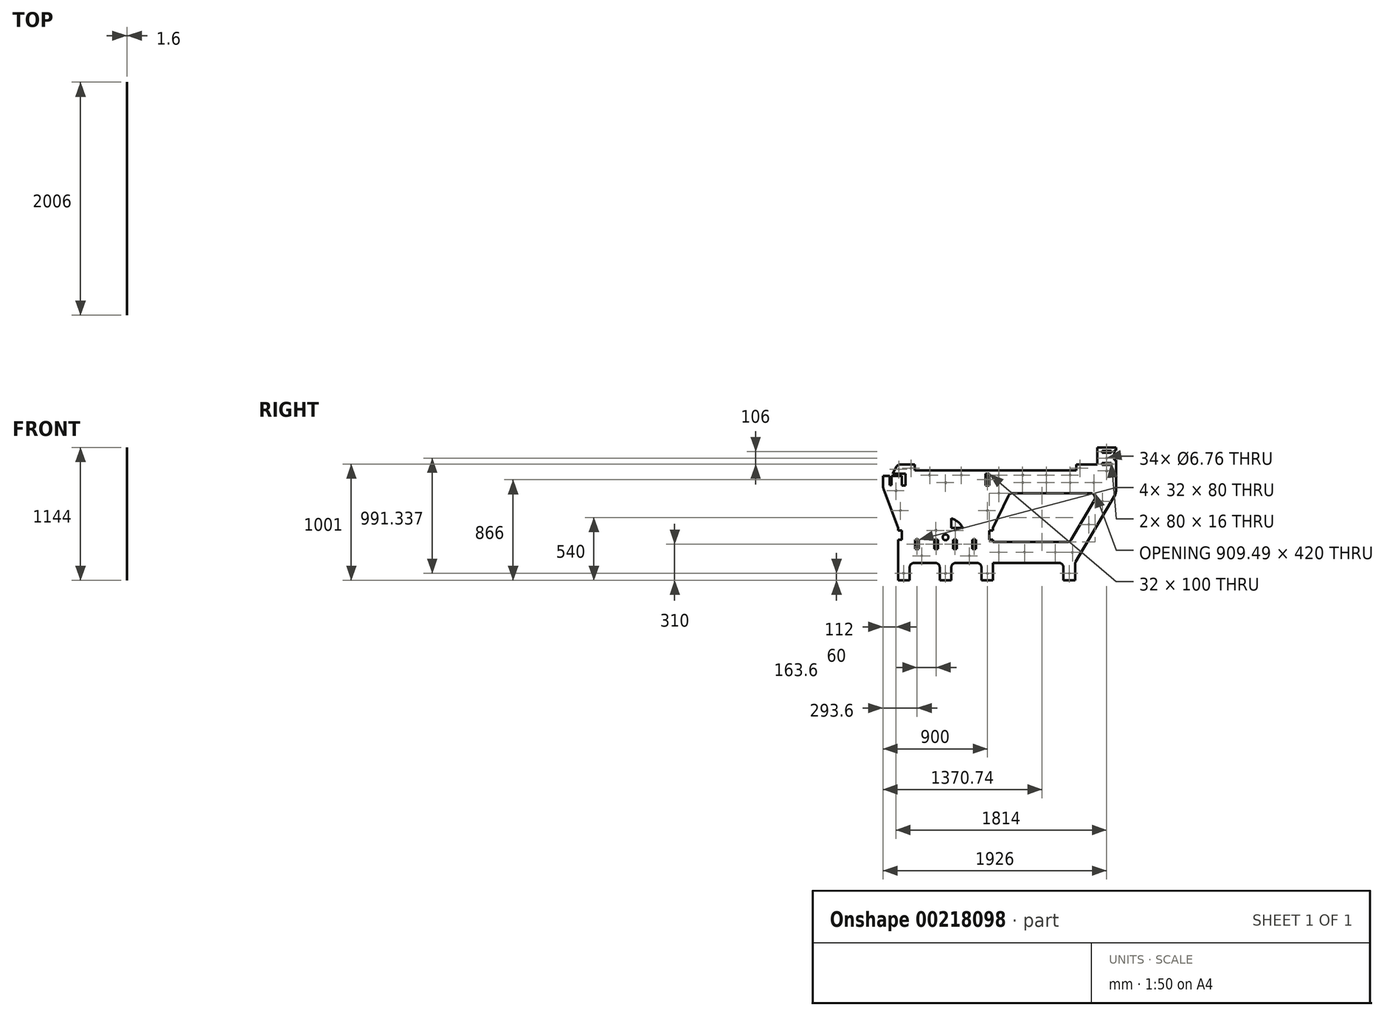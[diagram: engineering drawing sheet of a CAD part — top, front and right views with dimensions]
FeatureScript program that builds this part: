
annotation { "Feature Type Name" : "Feature", "Feature Type Description" : "" }
export const myFeature = defineFeature(function(context is Context, id is Id, definition is map)
    precondition{}
    {
        {
            assignVariable(context, id + "F0", {"name" : "grueso", "anyValue" : 1.6});
        }
        {
            var Q0;
            Q0=qCreatedBy(makeId("Right.planeOp"),FACE);
            var sketch = newSketch(context, id + "F1", { "sketchPlane" : qUnion([Q0])});
            skLineSegment(sketch, "E0.bottom", {"start": v(0, 0) * mm, "end": v(818, 0) * mm});
            skLineSegment(sketch, "E0.top", {"start": v(0, 900) * mm, "end": v(818, 900) * mm});
            skLineSegment(sketch, "E0.left", {"start": v(0, 0) * mm, "end": v(0, 900) * mm});
            skLineSegment(sketch, "E0.right", {"start": v(818, 0) * mm, "end": v(818, 900) * mm});
            skPoint(sketch, "E0.middle", {"position": v(409, 450) * mm});
            skLineSegment(sketch, "E1", {"start": v(100, 0) * mm, "end": v(100, 110) * mm});
            skLineSegment(sketch, "E2", {"start": v(140, 750) * mm, "end": v(678, 750) * mm});
            skLineSegment(sketch, "E3", {"start": v(718, 710) * mm, "end": v(718, 490) * mm});
            skPoint(sketch, "E4.visualSharp", {"position": v(100, 750) * mm});
            skArc(sketch, "E4.filletArc", {"start": v(140, 750) * mm, "mid": v(111.72, 738.28) * mm, "end": v(100, 710) * mm});
            skPoint(sketch, "E5.visualSharp", {"position": v(718, 750) * mm});
            skArc(sketch, "E5.filletArc", {"start": v(718, 710) * mm, "mid": v(706.28, 738.28) * mm, "end": v(678, 750) * mm});
            skLineSegment(sketch, "E6", {"start": v(678, 450) * mm, "end": v(619.82, 450) * mm});
            skLineSegment(sketch, "E7", {"start": v(678, 150) * mm, "end": v(626.89, 150) * mm});
            skLineSegment(sketch, "E8", {"start": v(32, 900) * mm, "end": v(32, 816) * mm});
            skLineSegment(sketch, "E9", {"start": v(32, 816) * mm, "end": v(64, 816) * mm});
            skLineSegment(sketch, "E10", {"start": v(64, 816) * mm, "end": v(64, 900) * mm});
            skLineSegment(sketch, "E11", {"start": v(409, -66.66) * mm, "end": v(409, 936.4) * mm, "construction": true});
            skPoint(sketch, "E11.endSnap0", {"position": v(409, 0) * mm});
            skLineSegment(sketch, "E12.trimOffspring", {"start": v(100, 490) * mm, "end": v(100, 710) * mm});
            skLineSegment(sketch, "E13.trimOffspring", {"start": v(718, 110) * mm, "end": v(718, 0) * mm});
            skPoint(sketch, "E14.visualSharp", {"position": v(718, 450) * mm});
            skArc(sketch, "E14.filletArc", {"start": v(678, 450) * mm, "mid": v(706.28, 461.72) * mm, "end": v(718, 490) * mm});
            skPoint(sketch, "E15.visualSharp", {"position": v(100, 450) * mm});
            skArc(sketch, "E15.filletArc", {"start": v(100, 490) * mm, "mid": v(111.72, 461.72) * mm, "end": v(140, 450) * mm});
            skPoint(sketch, "E16.visualSharp", {"position": v(100, 150) * mm});
            skArc(sketch, "E16.filletArc", {"start": v(140, 150) * mm, "mid": v(111.72, 138.28) * mm, "end": v(100, 110) * mm});
            skPoint(sketch, "E17.visualSharp", {"position": v(718, 150) * mm});
            skArc(sketch, "E17.filletArc", {"start": v(718, 110) * mm, "mid": v(706.28, 138.28) * mm, "end": v(678, 150) * mm});
            skLineSegment(sketch, "E18.MirrorCS", {"start": v(754, 816) * mm, "end": v(754, 900) * mm});
            skLineSegment(sketch, "E19.MirrorCS", {"start": v(786, 900) * mm, "end": v(786, 816) * mm});
            skLineSegment(sketch, "E20.MirrorCS", {"start": v(786, 816) * mm, "end": v(754, 816) * mm});
            skLineSegment(sketch, "E21.trimOffspring", {"start": v(603.68, 450) * mm, "end": v(140, 450) * mm});
            skLineSegment(sketch, "E22.trimOffspring", {"start": v(562.94, 150) * mm, "end": v(140, 150) * mm});
            skLineSegment(sketch, "E23", {"start": v(359, 61.01) * mm, "end": v(359, 0) * mm});
            skLineSegment(sketch, "E24", {"start": v(459, 110) * mm, "end": v(459, 0) * mm});
            skPoint(sketch, "E25.endSnap0", {"position": v(409, 900) * mm});
            skLineSegment(sketch, "E26", {"start": v(603.68, 450) * mm, "end": v(619.82, 450) * mm});
            skLineSegment(sketch, "E27", {"start": v(319, 150) * mm, "end": v(562.94, 150) * mm});
            skLineSegment(sketch, "E28", {"start": v(359, 110) * mm, "end": v(359, 61.01) * mm});
            skLineSegment(sketch, "E29", {"start": v(459, 110) * mm, "end": v(459, 110) * mm});
            skLineSegment(sketch, "E30", {"start": v(499, 150) * mm, "end": v(626.89, 150) * mm});
            skCircle(sketch, "E31", {"center": v(409, 370) * mm, "radius": 25 * mm});
            skPoint(sketch, "E32.visualSharp", {"position": v(459, 150) * mm});
            skArc(sketch, "E32.filletArc", {"start": v(499, 150) * mm, "mid": v(470.72, 138.28) * mm, "end": v(459, 110) * mm});
            skPoint(sketch, "E33.visualSharp", {"position": v(359, 150) * mm});
            skArc(sketch, "E33.filletArc", {"start": v(359, 110) * mm, "mid": v(347.28, 138.28) * mm, "end": v(319, 150) * mm});
            skLineSegment(sketch, "E34.bottom", {"start": v(32, 350) * mm, "end": v(0, 350) * mm});
            skLineSegment(sketch, "E34.top", {"start": v(32, 430) * mm, "end": v(0, 430) * mm});
            skLineSegment(sketch, "E34.left", {"start": v(32, 350) * mm, "end": v(32, 430) * mm});
            skLineSegment(sketch, "E34.right", {"start": v(0, 350) * mm, "end": v(0, 430) * mm});
            skLineSegment(sketch, "E35.MirrorCS", {"start": v(786, 350) * mm, "end": v(786, 430) * mm});
            skLineSegment(sketch, "E36.MirrorCS", {"start": v(786, 430) * mm, "end": v(818, 430) * mm});
            skLineSegment(sketch, "E37.MirrorCS", {"start": v(818, 350) * mm, "end": v(818, 430) * mm});
            skLineSegment(sketch, "E38.MirrorCS", {"start": v(786, 350) * mm, "end": v(818, 350) * mm});
            skLineSegment(sketch, "E39.bottom", {"start": v(179.6, 270) * mm, "end": v(147.6, 270) * mm});
            skLineSegment(sketch, "E39.top", {"start": v(179.6, 350) * mm, "end": v(147.6, 350) * mm});
            skLineSegment(sketch, "E39.left", {"start": v(179.6, 270) * mm, "end": v(179.6, 350) * mm});
            skLineSegment(sketch, "E39.right", {"start": v(147.6, 270) * mm, "end": v(147.6, 350) * mm});
            skPoint(sketch, "E39.middle", {"position": v(163.6, 310) * mm});
            skLineSegment(sketch, "E40", {"start": v(359, 750) * mm, "end": v(359, 450) * mm});
            skLineSegment(sketch, "E41", {"start": v(459, 750) * mm, "end": v(459, 450) * mm});
            skArc(sketch, "E42", {"start": v(359, 532.48) * mm, "mid": v(300.83, 501.15) * mm, "end": v(259, 450) * mm});
            skArc(sketch, "E43", {"start": v(459, 532.48) * mm, "mid": v(517.17, 501.15) * mm, "end": v(559, 450) * mm});
            skLineSegment(sketch, "E44.bottom", {"start": v(311.2, 270) * mm, "end": v(343.2, 270) * mm});
            skLineSegment(sketch, "E44.top", {"start": v(311.2, 350) * mm, "end": v(343.2, 350) * mm});
            skLineSegment(sketch, "E44.left", {"start": v(311.2, 270) * mm, "end": v(311.2, 350) * mm});
            skLineSegment(sketch, "E44.right", {"start": v(343.2, 270) * mm, "end": v(343.2, 350) * mm});
            skPoint(sketch, "E44.middle", {"position": v(327.2, 310) * mm});
            skPoint(sketch, "E45.cornerSnap0", {"position": v(327.2, 270) * mm});
            skLineSegment(sketch, "E46.bottom", {"start": v(474.8, 270) * mm, "end": v(506.8, 270) * mm});
            skLineSegment(sketch, "E46.top", {"start": v(474.8, 350) * mm, "end": v(506.8, 350) * mm});
            skLineSegment(sketch, "E46.left", {"start": v(474.8, 270) * mm, "end": v(474.8, 350) * mm});
            skLineSegment(sketch, "E46.right", {"start": v(506.8, 270) * mm, "end": v(506.8, 350) * mm});
            skPoint(sketch, "E46.middle", {"position": v(490.8, 310) * mm});
            skLineSegment(sketch, "E47.bottom", {"start": v(638.4, 270) * mm, "end": v(670.4, 270) * mm});
            skLineSegment(sketch, "E47.top", {"start": v(638.4, 350) * mm, "end": v(670.4, 350) * mm});
            skLineSegment(sketch, "E47.left", {"start": v(638.4, 270) * mm, "end": v(638.4, 350) * mm});
            skLineSegment(sketch, "E47.right", {"start": v(670.4, 270) * mm, "end": v(670.4, 350) * mm});
            skPoint(sketch, "E47.middle", {"position": v(654.4, 310) * mm});
            skLineSegment(sketch, "E48", {"start": v(818, 900) * mm, "end": v(1876, 900) * mm});
            skLineSegment(sketch, "E49", {"start": v(1876, 900) * mm, "end": v(1876, 760.86) * mm});
            skLineSegment(sketch, "E50", {"start": v(1870.5, 740.63) * mm, "end": v(1529.72, 159.37) * mm});
            skLineSegment(sketch, "E51", {"start": v(1524.23, 139.14) * mm, "end": v(1524.23, 0) * mm});
            skLineSegment(sketch, "E52", {"start": v(1524.23, 0) * mm, "end": v(1424.23, 0) * mm});
            skLineSegment(sketch, "E53", {"start": v(1424.23, 0) * mm, "end": v(1424.23, 110) * mm});
            skLineSegment(sketch, "E54", {"start": v(1690, 689.77) * mm, "end": v(1490.66, 349.77) * mm});
            skLineSegment(sketch, "E55", {"start": v(1456.15, 330) * mm, "end": v(818, 330) * mm});
            skLineSegment(sketch, "E56", {"start": v(949.82, 727.18) * mm, "end": v(818, 450) * mm});
            skPoint(sketch, "E57.visualSharp", {"position": v(1716.3, 734.63) * mm});
            skArc(sketch, "E57.filletArc", {"start": v(1690, 689.77) * mm, "mid": v(1690.2, 729.88) * mm, "end": v(1655.49, 750) * mm});
            skPoint(sketch, "E58.visualSharp", {"position": v(1424.23, 150) * mm});
            skArc(sketch, "E58.filletArc", {"start": v(1424.23, 110) * mm, "mid": v(1412.51, 138.28) * mm, "end": v(1384.23, 150) * mm});
            skPoint(sketch, "E59.visualSharp", {"position": v(1524.23, 150) * mm});
            skArc(sketch, "E59.filletArc", {"start": v(1529.72, 159.37) * mm, "mid": v(1525.63, 149.62) * mm, "end": v(1524.23, 139.14) * mm});
            skPoint(sketch, "E60.visualSharp", {"position": v(1876, 750) * mm});
            skArc(sketch, "E60.filletArc", {"start": v(1870.5, 740.63) * mm, "mid": v(1874.6, 750.38) * mm, "end": v(1876, 760.86) * mm});
            skArc(sketch, "E61.filletArc", {"start": v(1456.15, 330) * mm, "mid": v(1476.03, 335.3) * mm, "end": v(1490.66, 349.77) * mm});
            skLineSegment(sketch, "E62", {"start": v(1384.23, 150) * mm, "end": v(818, 150) * mm});
            skLineSegment(sketch, "E63", {"start": v(818, 450) * mm, "end": v(818, 330) * mm});
            skLineSegment(sketch, "E64", {"start": v(985.94, 750) * mm, "end": v(1655.49, 750) * mm});
            skPoint(sketch, "E65.visualSharp", {"position": v(960.67, 750) * mm});
            skArc(sketch, "E65.filletArc", {"start": v(985.94, 750) * mm, "mid": v(964.58, 743.82) * mm, "end": v(949.82, 727.18) * mm});
            skLineSegment(sketch, "E66", {"start": v(0, 900) * mm, "end": v(-130, 900) * mm});
            skLineSegment(sketch, "E67", {"start": v(-130, 900) * mm, "end": v(-130, 821.57) * mm});
            skPoint(sketch, "E68", {"position": v(0, 450) * mm});
            skLineSegment(sketch, "E69", {"start": v(-122.5, 779.78) * mm, "end": v(0, 450) * mm});
            skPoint(sketch, "E70.visualSharp", {"position": v(-130, 800) * mm});
            skArc(sketch, "E70.filletArc", {"start": v(-130, 821.57) * mm, "mid": v(-128.1, 800.34) * mm, "end": v(-122.5, 779.78) * mm});
            skLineSegment(sketch, "E71.bottom", {"start": v(-57, 820) * mm, "end": v(-73, 820) * mm});
            skLineSegment(sketch, "E71.top", {"start": v(-57, 900) * mm, "end": v(-73, 900) * mm});
            skLineSegment(sketch, "E71.left", {"start": v(-57, 820) * mm, "end": v(-57, 900) * mm});
            skLineSegment(sketch, "E71.right", {"start": v(-73, 820) * mm, "end": v(-73, 900) * mm});
            skPoint(sketch, "E71.middle", {"position": v(-65, 860) * mm});
            skLineSegment(sketch, "E72", {"start": v(15.91, 996) * mm, "end": v(143, 996) * mm});
            skLineSegment(sketch, "E73", {"start": v(786, 946) * mm, "end": v(1876, 946) * mm});
            skLineSegment(sketch, "E74", {"start": v(1876, 946) * mm, "end": v(1876, 900) * mm});
            skLineSegment(sketch, "E75", {"start": v(-48, 916) * mm, "end": v(-10, 981.12) * mm});
            skPoint(sketch, "E76.visualSharp", {"position": v(-1.32, 996) * mm});
            skArc(sketch, "E76.filletArc", {"start": v(15.91, 996) * mm, "mid": v(0.97, 992.02) * mm, "end": v(-10, 981.12) * mm});
            skLineSegment(sketch, "E77", {"start": v(143, 996) * mm, "end": v(143, 900) * mm});
            skLineSegment(sketch, "E78", {"start": v(143, 946) * mm, "end": v(754, 946) * mm});
            skLineSegment(sketch, "E79", {"start": v(754, 946) * mm, "end": v(786, 946) * mm});
            skLineSegment(sketch, "E80", {"start": v(786, 916) * mm, "end": v(786, 900) * mm});
            skLineSegment(sketch, "E81", {"start": v(754, 916) * mm, "end": v(754, 900) * mm});
            skLineSegment(sketch, "E82", {"start": v(754, 916) * mm, "end": v(786, 916) * mm});
            skLineSegment(sketch, "E83", {"start": v(1876, 946) * mm, "end": v(1876, 1160) * mm});
            skLineSegment(sketch, "E84", {"start": v(1876, 1160) * mm, "end": v(1716, 1160) * mm});
            skLineSegment(sketch, "E85", {"start": v(1716, 1160) * mm, "end": v(1716, 946) * mm});
            skLineSegment(sketch, "E86", {"start": v(-48, 916) * mm, "end": v(64, 916) * mm});
            skLineSegment(sketch, "E87", {"start": v(64, 916) * mm, "end": v(64, 900) * mm});
            skLineSegment(sketch, "E88", {"start": v(1716, 996) * mm, "end": v(1536, 996) * mm});
            skLineSegment(sketch, "E89", {"start": v(1536, 996) * mm, "end": v(1536, 946) * mm});
            skLineSegment(sketch, "E90", {"start": v(1756, 993) * mm, "end": v(1836, 993) * mm});
            skLineSegment(sketch, "E91", {"start": v(1836, 993) * mm, "end": v(1836, 1009) * mm});
            skLineSegment(sketch, "E92", {"start": v(1836, 1009) * mm, "end": v(1756, 1009) * mm});
            skLineSegment(sketch, "E93", {"start": v(1756, 1009) * mm, "end": v(1756, 993) * mm});
            skLineSegment(sketch, "E94", {"start": v(1756, 1099) * mm, "end": v(1836, 1099) * mm});
            skLineSegment(sketch, "E95", {"start": v(1836, 1099) * mm, "end": v(1836, 1115) * mm});
            skLineSegment(sketch, "E96", {"start": v(1836, 1115) * mm, "end": v(1756, 1115) * mm});
            skLineSegment(sketch, "E97", {"start": v(1756, 1115) * mm, "end": v(1756, 1099) * mm});
            skLineSegment(sketch, "E98", {"start": v(1716, 1144) * mm, "end": v(1876, 1144) * mm});
            skLineSegment(sketch, "E99", {"start": v(1876, 1116.5) * mm, "end": v(1860, 1116.5) * mm});
            skLineSegment(sketch, "E100", {"start": v(1860, 1116.5) * mm, "end": v(1860, 1036.5) * mm});
            skLineSegment(sketch, "E101", {"start": v(1860, 1036.5) * mm, "end": v(1876, 1036.5) * mm});
            skSolve(sketch);
        }
        {
            var Q0;
            {var subQ5=sQuery(id+"F1.wireOp",EDGE,"E48");Q0=makeQuery(id+"F1.imprint","IMPRINT",FACE,{"disambiguationData":[TD([[makeQuery(id+"F1.imprint","IMPRINT",EDGE,{"derivedFrom":subQ5}),-1.0]])]});}
            var Q1;
            {var subQ1=sQuery(id+"F1.wireOp",EDGE,"E23");Q1=makeQuery(id+"F1.imprint","IMPRINT",FACE,{"disambiguationData":[TD([[makeQuery(id+"F1.imprint","IMPRINT",EDGE,{"derivedFrom":subQ1}),1.0]])]});}
            var Q2;
            {var subQ34=sQuery(id+"F1.wireOp",EDGE,"E1");Q2=makeQuery(id+"F1.imprint","IMPRINT",FACE,{"disambiguationData":[TD([[makeQuery(id+"F1.imprint","IMPRINT",EDGE,{"derivedFrom":subQ34}),1.0]])]});}
            var Q3;
            {var subQ3=sQuery(id+"F1.wireOp",EDGE,"E42");Q3=makeQuery(id+"F1.imprint","IMPRINT",FACE,{"disambiguationData":[TD([[makeQuery(id+"F1.imprint","IMPRINT",EDGE,{"derivedFrom":subQ3}),1.0]])]});}
            var Q4;
            {var subQ3=sQuery(id+"F1.wireOp",EDGE,"E43");Q4=makeQuery(id+"F1.imprint","IMPRINT",FACE,{"disambiguationData":[TD([[makeQuery(id+"F1.imprint","IMPRINT",EDGE,{"derivedFrom":subQ3}),-1.0]])]});}
            var Q5;
            {var subQ0=sQuery(id+"F1.wireOp",EDGE,"E40");var subQ4=sQuery(id+"F1.wireOp",EDGE,"E2");var subQ5=makeQuery(id+"F1.imprint","INTERSECT",VERTEX,{"derivedFrom":[subQ4,subQ0]});Q5=makeQuery(id+"F1.imprint","IMPRINT",FACE,{"disambiguationData":[TD([[makeQuery(id+"F1.imprint","IMPRINT",EDGE,{"disambiguationData":[TD([[subQ5,-1.0]])],"derivedFrom":subQ4}),-1.0]])]});}
            var Q6;
            {var subQ1=sQuery(id+"F1.wireOp",EDGE,"E66");Q6=makeQuery(id+"F1.imprint","IMPRINT",FACE,{"disambiguationData":[TD([[makeQuery(id+"F1.imprint","IMPRINT",EDGE,{"derivedFrom":subQ1}),1.0]])]});}
            var Q7;
            {var subQ0=sQuery(id+"F1.wireOp",EDGE,"8OQY55YS-XfRK-lt9R-q8WZ-AcM36SrQRaeO");Q7=makeQuery(id+"F1.imprint","IMPRINT",FACE,{"disambiguationData":[TD([[makeQuery(id+"F1.imprint","IMPRINT",EDGE,{"derivedFrom":subQ0}),-1.0]])]});}
            var Q8;
            {var subQ1=sQuery(id+"F1.wireOp",EDGE,"E48");Q8=makeQuery(id+"F1.imprint","IMPRINT",FACE,{"disambiguationData":[TD([[makeQuery(id+"F1.imprint","IMPRINT",EDGE,{"derivedFrom":subQ1}),1.0]])]});}
            var Q9;
            {var subQ4=sQuery(id+"F1.wireOp",EDGE,"E78");Q9=makeQuery(id+"F1.imprint","IMPRINT",FACE,{"disambiguationData":[TD([[makeQuery(id+"F1.imprint","IMPRINT",EDGE,{"derivedFrom":subQ4}),-1.0]])]});}
            var Q10;
            {var subQ0=sQuery(id+"F1.wireOp",EDGE,"E72");Q10=makeQuery(id+"F1.imprint","IMPRINT",FACE,{"disambiguationData":[TD([[makeQuery(id+"F1.imprint","IMPRINT",EDGE,{"derivedFrom":subQ0}),-1.0]])]});}
            var Q11;
            {var subQ4=sQuery(id+"F1.wireOp",EDGE,"E88");Q11=makeQuery(id+"F1.imprint","IMPRINT",FACE,{"disambiguationData":[TD([[makeQuery(id+"F1.imprint","IMPRINT",EDGE,{"derivedFrom":subQ4}),1.0]])]});}
            var Q12;
            {var subQ0=sQuery(id+"F1.wireOp",EDGE,"E4.filletArc");Q12=makeQuery(id+"F1.imprint","IMPRINT",FACE,{"disambiguationData":[TD([[makeQuery(id+"F1.imprint","IMPRINT",EDGE,{"derivedFrom":subQ0}),1.0]])]});}
            var Q13;
            Q13=makeQuery(id+"F1.imprint","IMPRINT",FACE,{"disambiguationData":[TD([[makeQuery(id+"F1.imprint","IMPRINT",EDGE,{"derivedFrom":sQuery(id+"F1.wireOp",EDGE,"E3")}),-1.0]])]});
            var Q14;
            Q14=makeQuery(id+"F1.imprint","IMPRINT",FACE,{"disambiguationData":[TD([[makeQuery(id+"F1.imprint","IMPRINT",EDGE,{"derivedFrom":sQuery(id+"F1.wireOp",EDGE,"E90")}),-1.0]])]});
            extrude(context, id + "F2", {"entities" : qUnion([Q0, Q1, Q2, Q3, Q4, Q5, Q6, Q7, Q8, Q9, Q10, Q11, Q12, Q13, Q14]), "depth" : (getVariable(context, 'grueso')) * mm});
        }
        {
            var Q0;
            Q0=makeQuery(id+"F2.opExtrude","CAP_FACE",FACE,{"disambiguationData":[OSD([sQuery(id+"F1.wireOp",EDGE,"E0.bottom"),sQuery(id+"F1.wireOp",EDGE,"E0.top"),sQuery(id+"F1.wireOp",EDGE,"E0.left"),sQuery(id+"F1.wireOp",EDGE,"E0.right"),sQuery(id+"F1.wireOp",EDGE,"E1"),sQuery(id+"F1.wireOp",EDGE,"E2"),sQuery(id+"F1.wireOp",EDGE,"E3"),sQuery(id+"F1.wireOp",EDGE,"E4.filletArc"),sQuery(id+"F1.wireOp",EDGE,"E5.filletArc"),sQuery(id+"F1.wireOp",EDGE,"E6"),sQuery(id+"F1.wireOp",EDGE,"E7"),sQuery(id+"F1.wireOp",EDGE,"E8"),sQuery(id+"F1.wireOp",EDGE,"E9"),sQuery(id+"F1.wireOp",EDGE,"E10"),sQuery(id+"F1.wireOp",EDGE,"E12.trimOffspring"),sQuery(id+"F1.wireOp",EDGE,"E13.trimOffspring"),sQuery(id+"F1.wireOp",EDGE,"E14.filletArc"),sQuery(id+"F1.wireOp",EDGE,"E15.filletArc"),sQuery(id+"F1.wireOp",EDGE,"E16.filletArc"),sQuery(id+"F1.wireOp",EDGE,"E17.filletArc"),sQuery(id+"F1.wireOp",EDGE,"E18.MirrorCS"),sQuery(id+"F1.wireOp",EDGE,"E19.MirrorCS"),sQuery(id+"F1.wireOp",EDGE,"E20.MirrorCS"),sQuery(id+"F1.wireOp",EDGE,"E21.trimOffspring"),sQuery(id+"F1.wireOp",EDGE,"E22.trimOffspring"),sQuery(id+"F1.wireOp",EDGE,"E23"),sQuery(id+"F1.wireOp",EDGE,"E24"),sQuery(id+"F1.wireOp",EDGE,"E26"),sQuery(id+"F1.wireOp",EDGE,"E28"),sQuery(id+"F1.wireOp",EDGE,"E30"),sQuery(id+"F1.wireOp",EDGE,"E31"),sQuery(id+"F1.wireOp",EDGE,"E32.filletArc"),sQuery(id+"F1.wireOp",EDGE,"E33.filletArc"),sQuery(id+"F1.wireOp",EDGE,"E34.bottom"),sQuery(id+"F1.wireOp",EDGE,"E34.top"),sQuery(id+"F1.wireOp",EDGE,"E34.left"),sQuery(id+"F1.wireOp",EDGE,"E35.MirrorCS"),sQuery(id+"F1.wireOp",EDGE,"E36.MirrorCS"),sQuery(id+"F1.wireOp",EDGE,"E38.MirrorCS"),sQuery(id+"F1.wireOp",EDGE,"E39.bottom"),sQuery(id+"F1.wireOp",EDGE,"E39.top"),sQuery(id+"F1.wireOp",EDGE,"E39.left"),sQuery(id+"F1.wireOp",EDGE,"E39.right"),sQuery(id+"F1.wireOp",EDGE,"E40"),sQuery(id+"F1.wireOp",EDGE,"E41"),sQuery(id+"F1.wireOp",EDGE,"E42"),sQuery(id+"F1.wireOp",EDGE,"E43"),sQuery(id+"F1.wireOp",EDGE,"E44.bottom"),sQuery(id+"F1.wireOp",EDGE,"E44.top"),sQuery(id+"F1.wireOp",EDGE,"E44.left"),sQuery(id+"F1.wireOp",EDGE,"E44.right"),sQuery(id+"F1.wireOp",EDGE,"E46.bottom"),sQuery(id+"F1.wireOp",EDGE,"E46.top"),sQuery(id+"F1.wireOp",EDGE,"E46.left"),sQuery(id+"F1.wireOp",EDGE,"E46.right"),sQuery(id+"F1.wireOp",EDGE,"E47.bottom"),sQuery(id+"F1.wireOp",EDGE,"E47.top"),sQuery(id+"F1.wireOp",EDGE,"E47.left"),sQuery(id+"F1.wireOp",EDGE,"E47.right"),sQuery(id+"F1.wireOp",EDGE,"E49"),sQuery(id+"F1.wireOp",EDGE,"E50"),sQuery(id+"F1.wireOp",EDGE,"E51"),sQuery(id+"F1.wireOp",EDGE,"E52"),sQuery(id+"F1.wireOp",EDGE,"E53"),sQuery(id+"F1.wireOp",EDGE,"E54"),sQuery(id+"F1.wireOp",EDGE,"E55"),sQuery(id+"F1.wireOp",EDGE,"E56"),sQuery(id+"F1.wireOp",EDGE,"E57.filletArc"),sQuery(id+"F1.wireOp",EDGE,"E58.filletArc"),sQuery(id+"F1.wireOp",EDGE,"E59.filletArc"),sQuery(id+"F1.wireOp",EDGE,"E60.filletArc"),sQuery(id+"F1.wireOp",EDGE,"E61.filletArc"),sQuery(id+"F1.wireOp",EDGE,"E62"),sQuery(id+"F1.wireOp",EDGE,"E63"),sQuery(id+"F1.wireOp",EDGE,"E64"),sQuery(id+"F1.wireOp",EDGE,"E65.filletArc"),sQuery(id+"F1.wireOp",EDGE,"E66"),sQuery(id+"F1.wireOp",EDGE,"E67"),sQuery(id+"F1.wireOp",EDGE,"E69"),sQuery(id+"F1.wireOp",EDGE,"E70.filletArc"),sQuery(id+"F1.wireOp",EDGE,"E71.bottom"),sQuery(id+"F1.wireOp",EDGE,"E71.left"),sQuery(id+"F1.wireOp",EDGE,"E71.right"),sQuery(id+"F1.wireOp",EDGE,"E72"),sQuery(id+"F1.wireOp",EDGE,"E73"),sQuery(id+"F1.wireOp",EDGE,"E74"),sQuery(id+"F1.wireOp",EDGE,"E75"),sQuery(id+"F1.wireOp",EDGE,"E76.filletArc"),sQuery(id+"F1.wireOp",EDGE,"E77"),sQuery(id+"F1.wireOp",EDGE,"E78"),sQuery(id+"F1.wireOp",EDGE,"E79"),sQuery(id+"F1.wireOp",EDGE,"E80"),sQuery(id+"F1.wireOp",EDGE,"E81"),sQuery(id+"F1.wireOp",EDGE,"E82"),sQuery(id+"F1.wireOp",EDGE,"E83"),sQuery(id+"F1.wireOp",EDGE,"E84"),sQuery(id+"F1.wireOp",EDGE,"E85"),sQuery(id+"F1.wireOp",EDGE,"E86"),sQuery(id+"F1.wireOp",EDGE,"E87"),sQuery(id+"F1.wireOp",EDGE,"E88"),sQuery(id+"F1.wireOp",EDGE,"E89")])],"isStart":false});
            var sketch = newSketch(context, id + "F3", { "sketchPlane" : qUnion([Q0])});
            skPoint(sketch, "E102", {"position": v(7, 956) * mm});
            skPoint(sketch, "E103", {"position": v(272.67, 906) * mm});
            skPoint(sketch, "E104", {"position": v(545.33, 906) * mm});
            skPoint(sketch, "E105", {"position": v(868, 906) * mm});
            skPoint(sketch, "E106", {"position": v(1072.5, 906) * mm});
            skPoint(sketch, "E107", {"position": v(1277, 906) * mm});
            skPoint(sketch, "E108", {"position": v(1481.5, 906) * mm});
            skPoint(sketch, "E109", {"position": v(1566, 966) * mm});
            skPoint(sketch, "E110", {"position": v(868, 750) * mm});
            skPoint(sketch, "E111", {"position": v(-18, 770) * mm});
            skPoint(sketch, "E112", {"position": v(409, 840) * mm});
            skPoint(sketch, "E113", {"position": v(1072.5, 840) * mm});
            skPoint(sketch, "E114", {"position": v(1759.61, 680) * mm});
            skPoint(sketch, "E114.positionSnap0", {"position": v(1797.4, 771.34) * mm});
            skPoint(sketch, "E115", {"position": v(18.75, 600) * mm});
            skPoint(sketch, "E116", {"position": v(768, 600) * mm});
            skPoint(sketch, "E117", {"position": v(1642.36, 480) * mm});
            skPoint(sketch, "E118", {"position": v(325.44, 430) * mm});
            skPoint(sketch, "E119", {"position": v(492.56, 430) * mm});
            skPoint(sketch, "E120", {"position": v(204.5, 210) * mm});
            skPoint(sketch, "E120.positionSnap0", {"position": v(229.5, 150) * mm});
            skPoint(sketch, "E121", {"position": v(613.5, 210) * mm});
            skPoint(sketch, "E121.positionSnap0", {"position": v(588.5, 150) * mm});
            skPoint(sketch, "E122", {"position": v(50, 60) * mm});
            skPoint(sketch, "E122.positionSnap0", {"position": v(50, 0) * mm});
            skPoint(sketch, "E123", {"position": v(409, 60) * mm});
            skPoint(sketch, "E123.positionSnap0", {"position": v(409, 0) * mm});
            skPoint(sketch, "E124", {"position": v(768, 60) * mm});
            skPoint(sketch, "E124.positionSnap0", {"position": v(768, 0) * mm});
            skPoint(sketch, "E125", {"position": v(1474.23, 60) * mm});
            skPoint(sketch, "E125.positionSnap0", {"position": v(1474.23, 0) * mm});
            skPoint(sketch, "E126", {"position": v(868, 240) * mm});
            skPoint(sketch, "E127", {"position": v(1090.67, 240) * mm});
            skPoint(sketch, "E127.positionSnap0", {"position": v(1101.11, 150) * mm});
            skPoint(sketch, "E128", {"position": v(1354.23, 240) * mm});
            skPoint(sketch, "E129", {"position": v(1501.65, 240) * mm});
            skPoint(sketch, "E130", {"position": v(1277, 840) * mm});
            skPoint(sketch, "E131", {"position": v(1481.5, 840) * mm});
            skPoint(sketch, "E132", {"position": v(1686, 840) * mm});
            skPoint(sketch, "E133", {"position": v(1796, 1051.34) * mm});
            skPoint(sketch, "E134", {"position": v(1796, 941.34) * mm});
            skPoint(sketch, "E135", {"position": v(113, 966) * mm});
            skSolve(sketch);
        }
        {
            var Q0;
            Q0=sQuery(id+"F3.wireOp",VERTEX,"E102");
            var Q1;
            Q1=sQuery(id+"F3.wireOp",VERTEX,"E103");
            var Q2;
            Q2=sQuery(id+"F3.wireOp",VERTEX,"E104");
            var Q3;
            Q3=sQuery(id+"F3.wireOp",VERTEX,"E105");
            var Q4;
            Q4=sQuery(id+"F3.wireOp",VERTEX,"E106");
            var Q5;
            Q5=sQuery(id+"F3.wireOp",VERTEX,"E107");
            var Q6;
            Q6=sQuery(id+"F3.wireOp",VERTEX,"E108");
            var Q7;
            Q7=sQuery(id+"F3.wireOp",VERTEX,"E109");
            var Q8;
            Q8=sQuery(id+"F3.wireOp",VERTEX,"8da9923a-48d6-4ca7-8e1d-4f904342daaa");
            var Q9;
            Q9=sQuery(id+"F3.wireOp",VERTEX,"E113");
            var Q10;
            Q10=sQuery(id+"F3.wireOp",VERTEX,"E112");
            var Q11;
            Q11=sQuery(id+"F3.wireOp",VERTEX,"E111");
            var Q12;
            Q12=sQuery(id+"F3.wireOp",VERTEX,"E110");
            var Q13;
            Q13=sQuery(id+"F3.wireOp",VERTEX,"E114");
            var Q14;
            Q14=sQuery(id+"F3.wireOp",VERTEX,"E116");
            var Q15;
            Q15=sQuery(id+"F3.wireOp",VERTEX,"E115");
            var Q16;
            Q16=sQuery(id+"F3.wireOp",VERTEX,"E118");
            var Q17;
            Q17=sQuery(id+"F3.wireOp",VERTEX,"E119");
            var Q18;
            Q18=sQuery(id+"F3.wireOp",VERTEX,"E120");
            var Q19;
            Q19=sQuery(id+"F3.wireOp",VERTEX,"E121");
            var Q20;
            Q20=sQuery(id+"F3.wireOp",VERTEX,"E123");
            var Q21;
            Q21=sQuery(id+"F3.wireOp",VERTEX,"E122");
            var Q22;
            Q22=sQuery(id+"F3.wireOp",VERTEX,"E124");
            var Q23;
            Q23=sQuery(id+"F3.wireOp",VERTEX,"E126");
            var Q24;
            Q24=sQuery(id+"F3.wireOp",VERTEX,"E127");
            var Q25;
            Q25=sQuery(id+"F3.wireOp",VERTEX,"E128");
            var Q26;
            Q26=sQuery(id+"F3.wireOp",VERTEX,"E125");
            var Q27;
            Q27=sQuery(id+"F3.wireOp",VERTEX,"E129");
            var Q28;
            Q28=sQuery(id+"F3.wireOp",VERTEX,"E117");
            var Q29;
            Q29=sQuery(id+"F3.wireOp",VERTEX,"E130");
            var Q30;
            Q30=sQuery(id+"F3.wireOp",VERTEX,"E131");
            var Q31;
            Q31=sQuery(id+"F3.wireOp",VERTEX,"E132");
            var Q32;
            Q32=sQuery(id+"F3.wireOp",VERTEX,"E133");
            var Q33;
            Q33=sQuery(id+"F3.wireOp",VERTEX,"E134");
            var Q34;
            Q34=sQuery(id+"F3.wireOp",VERTEX,"E135");
            var Q35;
            Q35=makeQuery(id+"F2.opExtrude","SWEPT_BODY",BODY,{"disambiguationData":[OSD([sQuery(id+"F1.wireOp",EDGE,"E0.bottom"),sQuery(id+"F1.wireOp",EDGE,"E0.top"),sQuery(id+"F1.wireOp",EDGE,"E0.left"),sQuery(id+"F1.wireOp",EDGE,"E0.right"),sQuery(id+"F1.wireOp",EDGE,"E1"),sQuery(id+"F1.wireOp",EDGE,"E2"),sQuery(id+"F1.wireOp",EDGE,"E3"),sQuery(id+"F1.wireOp",EDGE,"E4.filletArc"),sQuery(id+"F1.wireOp",EDGE,"E5.filletArc"),sQuery(id+"F1.wireOp",EDGE,"E6"),sQuery(id+"F1.wireOp",EDGE,"E7"),sQuery(id+"F1.wireOp",EDGE,"E8"),sQuery(id+"F1.wireOp",EDGE,"E9"),sQuery(id+"F1.wireOp",EDGE,"E10"),sQuery(id+"F1.wireOp",EDGE,"E12.trimOffspring"),sQuery(id+"F1.wireOp",EDGE,"E13.trimOffspring"),sQuery(id+"F1.wireOp",EDGE,"E14.filletArc"),sQuery(id+"F1.wireOp",EDGE,"E15.filletArc"),sQuery(id+"F1.wireOp",EDGE,"E16.filletArc"),sQuery(id+"F1.wireOp",EDGE,"E17.filletArc"),sQuery(id+"F1.wireOp",EDGE,"E18.MirrorCS"),sQuery(id+"F1.wireOp",EDGE,"E19.MirrorCS"),sQuery(id+"F1.wireOp",EDGE,"E20.MirrorCS"),sQuery(id+"F1.wireOp",EDGE,"E21.trimOffspring"),sQuery(id+"F1.wireOp",EDGE,"E22.trimOffspring"),sQuery(id+"F1.wireOp",EDGE,"E23"),sQuery(id+"F1.wireOp",EDGE,"E24"),sQuery(id+"F1.wireOp",EDGE,"E26"),sQuery(id+"F1.wireOp",EDGE,"E28"),sQuery(id+"F1.wireOp",EDGE,"E30"),sQuery(id+"F1.wireOp",EDGE,"E31"),sQuery(id+"F1.wireOp",EDGE,"E32.filletArc"),sQuery(id+"F1.wireOp",EDGE,"E33.filletArc"),sQuery(id+"F1.wireOp",EDGE,"E34.bottom"),sQuery(id+"F1.wireOp",EDGE,"E34.top"),sQuery(id+"F1.wireOp",EDGE,"E34.left"),sQuery(id+"F1.wireOp",EDGE,"E35.MirrorCS"),sQuery(id+"F1.wireOp",EDGE,"E36.MirrorCS"),sQuery(id+"F1.wireOp",EDGE,"E38.MirrorCS"),sQuery(id+"F1.wireOp",EDGE,"E39.bottom"),sQuery(id+"F1.wireOp",EDGE,"E39.top"),sQuery(id+"F1.wireOp",EDGE,"E39.left"),sQuery(id+"F1.wireOp",EDGE,"E39.right"),sQuery(id+"F1.wireOp",EDGE,"E40"),sQuery(id+"F1.wireOp",EDGE,"E41"),sQuery(id+"F1.wireOp",EDGE,"E42"),sQuery(id+"F1.wireOp",EDGE,"E43"),sQuery(id+"F1.wireOp",EDGE,"E44.bottom"),sQuery(id+"F1.wireOp",EDGE,"E44.top"),sQuery(id+"F1.wireOp",EDGE,"E44.left"),sQuery(id+"F1.wireOp",EDGE,"E44.right"),sQuery(id+"F1.wireOp",EDGE,"E46.bottom"),sQuery(id+"F1.wireOp",EDGE,"E46.top"),sQuery(id+"F1.wireOp",EDGE,"E46.left"),sQuery(id+"F1.wireOp",EDGE,"E46.right"),sQuery(id+"F1.wireOp",EDGE,"E47.bottom"),sQuery(id+"F1.wireOp",EDGE,"E47.top"),sQuery(id+"F1.wireOp",EDGE,"E47.left"),sQuery(id+"F1.wireOp",EDGE,"E47.right"),sQuery(id+"F1.wireOp",EDGE,"E49"),sQuery(id+"F1.wireOp",EDGE,"E50"),sQuery(id+"F1.wireOp",EDGE,"E51"),sQuery(id+"F1.wireOp",EDGE,"E52"),sQuery(id+"F1.wireOp",EDGE,"E53"),sQuery(id+"F1.wireOp",EDGE,"E54"),sQuery(id+"F1.wireOp",EDGE,"E55"),sQuery(id+"F1.wireOp",EDGE,"E56"),sQuery(id+"F1.wireOp",EDGE,"E57.filletArc"),sQuery(id+"F1.wireOp",EDGE,"E58.filletArc"),sQuery(id+"F1.wireOp",EDGE,"E59.filletArc"),sQuery(id+"F1.wireOp",EDGE,"E60.filletArc"),sQuery(id+"F1.wireOp",EDGE,"E61.filletArc"),sQuery(id+"F1.wireOp",EDGE,"E62"),sQuery(id+"F1.wireOp",EDGE,"E63"),sQuery(id+"F1.wireOp",EDGE,"E64"),sQuery(id+"F1.wireOp",EDGE,"E65.filletArc"),sQuery(id+"F1.wireOp",EDGE,"E66"),sQuery(id+"F1.wireOp",EDGE,"E67"),sQuery(id+"F1.wireOp",EDGE,"E69"),sQuery(id+"F1.wireOp",EDGE,"E70.filletArc"),sQuery(id+"F1.wireOp",EDGE,"E71.bottom"),sQuery(id+"F1.wireOp",EDGE,"E71.left"),sQuery(id+"F1.wireOp",EDGE,"E71.right"),sQuery(id+"F1.wireOp",EDGE,"E72"),sQuery(id+"F1.wireOp",EDGE,"E73"),sQuery(id+"F1.wireOp",EDGE,"E74"),sQuery(id+"F1.wireOp",EDGE,"E75"),sQuery(id+"F1.wireOp",EDGE,"E76.filletArc"),sQuery(id+"F1.wireOp",EDGE,"E77"),sQuery(id+"F1.wireOp",EDGE,"E78"),sQuery(id+"F1.wireOp",EDGE,"E79"),sQuery(id+"F1.wireOp",EDGE,"E80"),sQuery(id+"F1.wireOp",EDGE,"E81"),sQuery(id+"F1.wireOp",EDGE,"E82"),sQuery(id+"F1.wireOp",EDGE,"E83"),sQuery(id+"F1.wireOp",EDGE,"E84"),sQuery(id+"F1.wireOp",EDGE,"E85"),sQuery(id+"F1.wireOp",EDGE,"E86"),sQuery(id+"F1.wireOp",EDGE,"E87"),sQuery(id+"F1.wireOp",EDGE,"E88"),sQuery(id+"F1.wireOp",EDGE,"E89")])]});
            hole(context, id + "F4", {"style" : HoleStyle.SIMPLE, "endStyle" : HoleEndStyle.THROUGH, "standardTappedOrClearance" : lookupTablePath({ "standard" : "ANSI", "fit" : "Normal (ASME)", "size" : "1/4", "type" : "Clearance" }), "standardBlindInLast" : lookupTablePath({ "fit" : "Free", "standard" : "ANSI", "size" : "1/4", "type" : "Clearance" }), "holeDiameter" : 6.76 * mm, "startFromSketch" : true, "locations" : qUnion([Q0, Q1, Q2, Q3, Q4, Q5, Q6, Q7, Q8, Q9, Q10, Q11, Q12, Q13, Q14, Q15, Q16, Q17, Q18, Q19, Q20, Q21, Q22, Q23, Q24, Q25, Q26, Q27, Q28, Q29, Q30, Q31, Q32, Q33, Q34]), "scope" : qUnion([Q35]), "isTappedThrough" : true});
        }
    });
